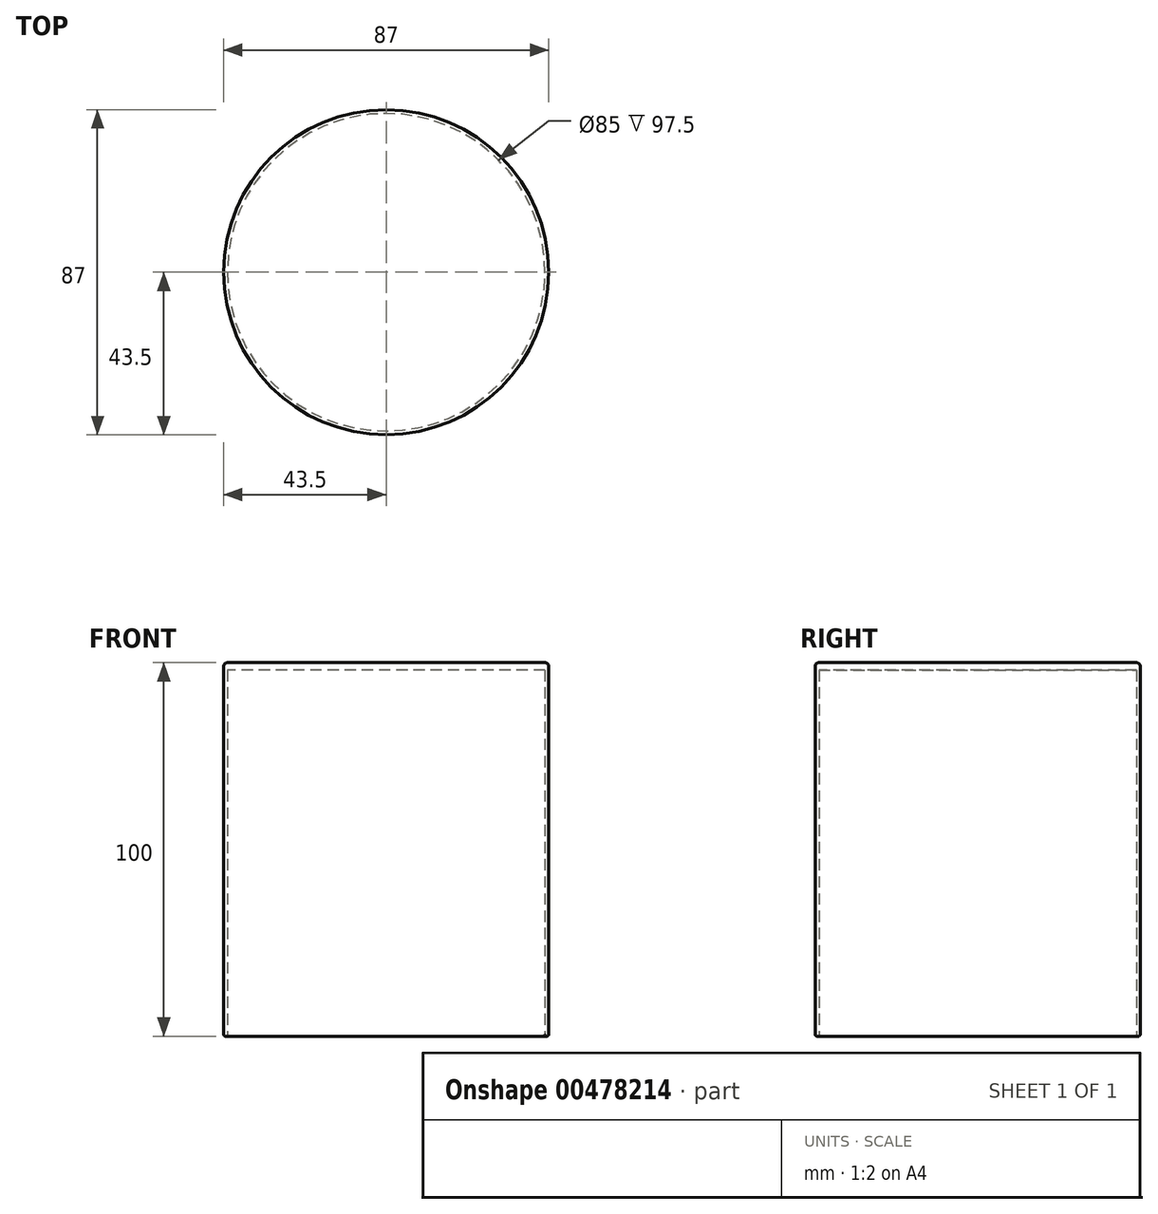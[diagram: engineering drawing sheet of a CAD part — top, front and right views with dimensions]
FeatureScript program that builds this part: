
annotation { "Feature Type Name" : "Feature", "Feature Type Description" : "" }
export const myFeature = defineFeature(function(context is Context, id is Id, definition is map)
    precondition{}
    {
        {
            var Q0;
            Q0=qCreatedBy(makeId("Top.planeOp"),FACE);
            var sketch = newSketch(context, id + "F0", { "sketchPlane" : qUnion([Q0])});
            skCircle(sketch, "E0", {"center": v(0, 0) * mm, "radius": 42.5 * mm});
            skCircle(sketch, "E1.0", {"center": v(0, 0) * mm, "radius": 43.5 * mm});
            skSolve(sketch);
        }
        {
            var Q0;
            Q0=qSketchRegion(id+"F0",true);
            extrude(context, id + "F1", {"entities" : qUnion([Q0]), "depth" : 100 * mm});
        }
        {
            var Q0;
            Q0=makeQuery(id+"F1.opExtrude","CAP_FACE",FACE,{"disambiguationData":[OSD([sQuery(id+"F0.wireOp",EDGE,"E0"),sQuery(id+"F0.wireOp",EDGE,"E1.0")])],"isStart":false});
            var sketch = newSketch(context, id + "F2", { "sketchPlane" : qUnion([Q0])});
            skCircle(sketch, "E2", {"center": v(0, 0) * mm, "radius": 43.5 * mm});
            skSolve(sketch);
        }
        {
            var Q0;
            Q0=qSketchRegion(id+"F2",true);
            extrude(context, id + "F3", {"entities" : qUnion([Q0]), "operationType" : NewBodyOperationType.ADD, "oppositeDirection" : true, "depth" : 2 * mm});
        }
        {
            var Q0;
            Q0=makeQuery(id+"F1.opExtrude","CAP_EDGE",EDGE,{"disambiguationData":[OSD([sQuery(id+"F0.wireOp",EDGE,"E1.0")])],"isStart":false});
            fillet(context, id + "F4", {"entities" : qUnion([Q0]), "radius" : 1 * mm, "tangentPropagation" : true, "allowEdgeOverflow" : false});
        }
        {
            var Q0;
            Q0=makeQuery(id+"F1.opExtrude","CAP_FACE",FACE,{"disambiguationData":[OSD([sQuery(id+"F0.wireOp",EDGE,"E0"),sQuery(id+"F0.wireOp",EDGE,"E1.0")])],"isStart":true});
            fillet(context, id + "F5", {"entities" : qUnion([Q0]), "radius" : .5 * mm, "tangentPropagation" : true, "allowEdgeOverflow" : false});
        }
    });
